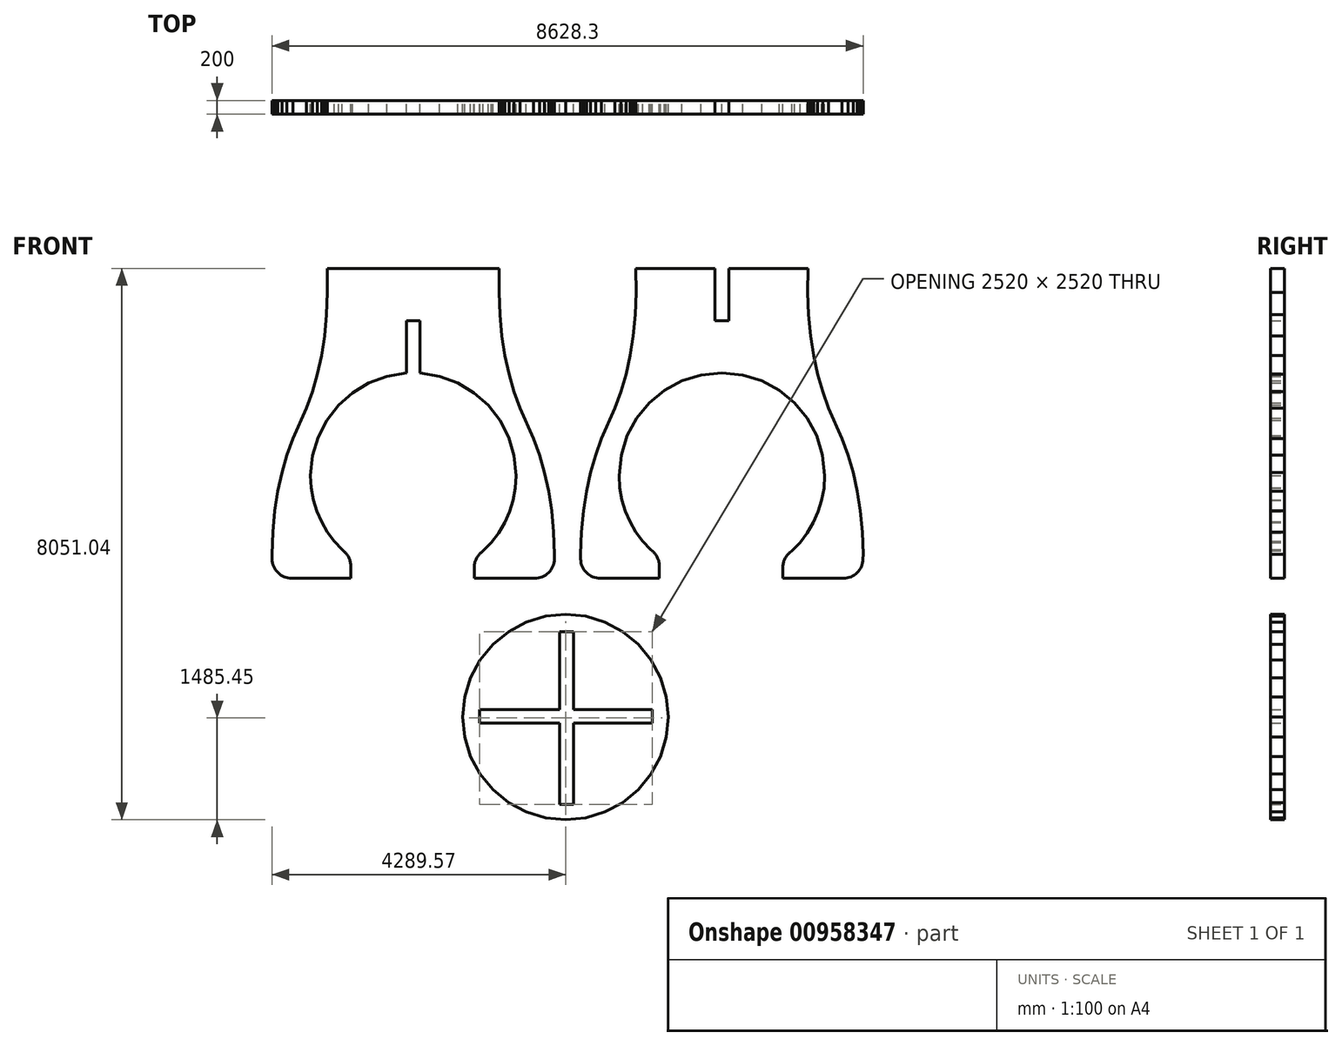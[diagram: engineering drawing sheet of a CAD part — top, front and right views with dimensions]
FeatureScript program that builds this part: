
annotation { "Feature Type Name" : "Feature", "Feature Type Description" : "" }
export const myFeature = defineFeature(function(context is Context, id is Id, definition is map)
    precondition{}
    {
        {
            var Q0;
            Q0=qCreatedBy(makeId("Front.planeOp"),FACE);
            var sketch = newSketch(context, id + "F0", { "sketchPlane" : qUnion([Q0])});
            skLineSegment(sketch, "E0", {"start": v(-5472.14, -2386.2) * mm, "end": v(-5169.83, -2416.68) * mm});
            skLineSegment(sketch, "E1", {"start": v(-5169.83, -2416.68) * mm, "end": v(-4888.27, -2504.08) * mm});
            skLineSegment(sketch, "E2", {"start": v(-4888.27, -2504.08) * mm, "end": v(-4633.47, -2642.38) * mm});
            skLineSegment(sketch, "E3", {"start": v(-4633.47, -2642.38) * mm, "end": v(-4411.48, -2825.54) * mm});
            skLineSegment(sketch, "E4", {"start": v(-4411.48, -2825.54) * mm, "end": v(-4228.31, -3047.54) * mm});
            skLineSegment(sketch, "E5", {"start": v(-4228.31, -3047.54) * mm, "end": v(-4090.01, -3302.33) * mm});
            skLineSegment(sketch, "E6", {"start": v(-4090.01, -3302.33) * mm, "end": v(-4002.61, -3583.9) * mm});
            skLineSegment(sketch, "E7", {"start": v(-4002.61, -3583.9) * mm, "end": v(-3972.14, -3886.2) * mm});
            skLineSegment(sketch, "E8", {"start": v(-3972.14, -3886.2) * mm, "end": v(-3983.21, -4069.37) * mm});
            skLineSegment(sketch, "E9", {"start": v(-3983.21, -4069.37) * mm, "end": v(-4015.57, -4245.97) * mm});
            skLineSegment(sketch, "E10", {"start": v(-4015.57, -4245.97) * mm, "end": v(-4067.92, -4414.7) * mm});
            skLineSegment(sketch, "E11", {"start": v(-4067.92, -4414.7) * mm, "end": v(-4138.96, -4574.27) * mm});
            skLineSegment(sketch, "E12", {"start": v(-4138.96, -4574.27) * mm, "end": v(-4227.4, -4723.4) * mm});
            skLineSegment(sketch, "E13", {"start": v(-4227.4, -4723.4) * mm, "end": v(-4331.93, -4860.76) * mm});
            skLineSegment(sketch, "E14", {"start": v(-4331.93, -4860.76) * mm, "end": v(-4451.26, -4985.1) * mm});
            skLineSegment(sketch, "E15", {"start": v(-4451.26, -4985.1) * mm, "end": v(-4584.1, -5095.1) * mm});
            skLineSegment(sketch, "E16", {"start": v(-4584.1, -5095.1) * mm, "end": v(-4584.1, -5386.56) * mm});
            skLineSegment(sketch, "E17", {"start": v(-4584.1, -5386.56) * mm, "end": v(-3416.13, -5386.56) * mm});
            skLineSegment(sketch, "E18", {"start": v(-3416.13, -5386.56) * mm, "end": v(-3411.1, -5036.82) * mm});
            skLineSegment(sketch, "E19", {"start": v(-3411.1, -5036.82) * mm, "end": v(-3423.6, -4708.36) * mm});
            skLineSegment(sketch, "E20", {"start": v(-3423.6, -4708.36) * mm, "end": v(-3452.73, -4400.09) * mm});
            skLineSegment(sketch, "E21", {"start": v(-3452.73, -4400.09) * mm, "end": v(-3497.58, -4110.9) * mm});
            skLineSegment(sketch, "E22", {"start": v(-3497.58, -4110.9) * mm, "end": v(-3557.24, -3839.7) * mm});
            skLineSegment(sketch, "E23", {"start": v(-3557.24, -3839.7) * mm, "end": v(-3630.82, -3585.4) * mm});
            skLineSegment(sketch, "E24", {"start": v(-3630.82, -3585.4) * mm, "end": v(-3717.4, -3346.9) * mm});
            skLineSegment(sketch, "E25", {"start": v(-3717.4, -3346.9) * mm, "end": v(-3816.1, -3123.12) * mm});
            skLineSegment(sketch, "E26", {"start": v(-3816.1, -3123.12) * mm, "end": v(-3914.8, -2899.32) * mm});
            skLineSegment(sketch, "E27", {"start": v(-3914.8, -2899.32) * mm, "end": v(-4001.4, -2660.83) * mm});
            skLineSegment(sketch, "E28", {"start": v(-4001.4, -2660.83) * mm, "end": v(-4074.97, -2406.53) * mm});
            skLineSegment(sketch, "E29", {"start": v(-4074.97, -2406.53) * mm, "end": v(-4134.64, -2135.33) * mm});
            skLineSegment(sketch, "E30", {"start": v(-4134.64, -2135.33) * mm, "end": v(-4179.48, -1846.15) * mm});
            skLineSegment(sketch, "E31", {"start": v(-4179.48, -1846.15) * mm, "end": v(-4208.6, -1537.87) * mm});
            skLineSegment(sketch, "E32", {"start": v(-4208.6, -1537.87) * mm, "end": v(-4221.11, -1209.4) * mm});
            skLineSegment(sketch, "E33", {"start": v(-4221.11, -1209.4) * mm, "end": v(-4216.09, -859.67) * mm});
            skLineSegment(sketch, "E34", {"start": v(-4216.09, -859.67) * mm, "end": v(-5372.12, -859.67) * mm});
            skLineSegment(sketch, "E35", {"start": v(-5372.12, -859.67) * mm, "end": v(-5372.12, -1622.94) * mm});
            skLineSegment(sketch, "E36", {"start": v(-5372.12, -1622.94) * mm, "end": v(-5572.12, -1622.94) * mm});
            skLineSegment(sketch, "E37", {"start": v(-5572.12, -1622.94) * mm, "end": v(-5572.12, -859.67) * mm});
            skLineSegment(sketch, "E38", {"start": v(-5572.12, -859.67) * mm, "end": v(-6730.15, -859.67) * mm});
            skLineSegment(sketch, "E39", {"start": v(-6730.15, -859.67) * mm, "end": v(-6725.13, -1209.4) * mm});
            skLineSegment(sketch, "E40", {"start": v(-6725.13, -1209.4) * mm, "end": v(-6737.64, -1537.87) * mm});
            skLineSegment(sketch, "E41", {"start": v(-6737.64, -1537.87) * mm, "end": v(-6766.76, -1846.15) * mm});
            skLineSegment(sketch, "E42", {"start": v(-6766.76, -1846.15) * mm, "end": v(-6811.6, -2135.33) * mm});
            skLineSegment(sketch, "E43", {"start": v(-6811.6, -2135.33) * mm, "end": v(-6871.27, -2406.53) * mm});
            skLineSegment(sketch, "E44", {"start": v(-6871.27, -2406.53) * mm, "end": v(-6944.85, -2660.83) * mm});
            skLineSegment(sketch, "E45", {"start": v(-6944.85, -2660.83) * mm, "end": v(-7031.44, -2899.32) * mm});
            skLineSegment(sketch, "E46", {"start": v(-7031.44, -2899.32) * mm, "end": v(-7130.14, -3123.12) * mm});
            skLineSegment(sketch, "E47", {"start": v(-7130.14, -3123.12) * mm, "end": v(-7228.84, -3346.9) * mm});
            skLineSegment(sketch, "E48", {"start": v(-7228.84, -3346.9) * mm, "end": v(-7315.42, -3585.4) * mm});
            skLineSegment(sketch, "E49", {"start": v(-7315.42, -3585.4) * mm, "end": v(-7389, -3839.7) * mm});
            skLineSegment(sketch, "E50", {"start": v(-7389, -3839.7) * mm, "end": v(-7448.66, -4110.9) * mm});
            skLineSegment(sketch, "E51", {"start": v(-7448.66, -4110.9) * mm, "end": v(-7493.5, -4400.09) * mm});
            skLineSegment(sketch, "E52", {"start": v(-7493.5, -4400.09) * mm, "end": v(-7522.63, -4708.36) * mm});
            skLineSegment(sketch, "E53", {"start": v(-7522.63, -4708.36) * mm, "end": v(-7535.14, -5036.82) * mm});
            skLineSegment(sketch, "E54", {"start": v(-7535.14, -5036.82) * mm, "end": v(-7530.12, -5386.56) * mm});
            skLineSegment(sketch, "E55", {"start": v(-7530.12, -5386.56) * mm, "end": v(-6384.1, -5386.56) * mm});
            skLineSegment(sketch, "E56", {"start": v(-6384.1, -5386.56) * mm, "end": v(-6384.1, -5077.1) * mm});
            skLineSegment(sketch, "E57", {"start": v(-6384.1, -5077.1) * mm, "end": v(-6512, -4967.11) * mm});
            skLineSegment(sketch, "E58", {"start": v(-6512, -4967.11) * mm, "end": v(-6626.8, -4843.6) * mm});
            skLineSegment(sketch, "E59", {"start": v(-6626.8, -4843.6) * mm, "end": v(-6727.26, -4707.77) * mm});
            skLineSegment(sketch, "E60", {"start": v(-6727.26, -4707.77) * mm, "end": v(-6812.18, -4560.83) * mm});
            skLineSegment(sketch, "E61", {"start": v(-6812.18, -4560.83) * mm, "end": v(-6880.34, -4404) * mm});
            skLineSegment(sketch, "E62", {"start": v(-6880.34, -4404) * mm, "end": v(-6930.53, -4238.47) * mm});
            skLineSegment(sketch, "E63", {"start": v(-6930.53, -4238.47) * mm, "end": v(-6961.53, -4065.47) * mm});
            skLineSegment(sketch, "E64", {"start": v(-6961.53, -4065.47) * mm, "end": v(-6972.14, -3886.2) * mm});
            skLineSegment(sketch, "E65", {"start": v(-6972.14, -3886.2) * mm, "end": v(-6941.66, -3583.9) * mm});
            skLineSegment(sketch, "E66", {"start": v(-6941.66, -3583.9) * mm, "end": v(-6854.26, -3302.33) * mm});
            skLineSegment(sketch, "E67", {"start": v(-6854.26, -3302.33) * mm, "end": v(-6715.96, -3047.54) * mm});
            skLineSegment(sketch, "E68", {"start": v(-6715.96, -3047.54) * mm, "end": v(-6532.8, -2825.54) * mm});
            skLineSegment(sketch, "E69", {"start": v(-6532.8, -2825.54) * mm, "end": v(-6310.8, -2642.38) * mm});
            skLineSegment(sketch, "E70", {"start": v(-6310.8, -2642.38) * mm, "end": v(-6056, -2504.08) * mm});
            skLineSegment(sketch, "E71", {"start": v(-6056, -2504.08) * mm, "end": v(-5774.44, -2416.68) * mm});
            skLineSegment(sketch, "E72", {"start": v(-5774.44, -2416.68) * mm, "end": v(-5472.14, -2386.2) * mm});
            skLineSegment(sketch, "E73", {"start": v(-9877.4, -2389.54) * mm, "end": v(-9592.6, -2435.87) * mm});
            skLineSegment(sketch, "E74", {"start": v(-9592.6, -2435.87) * mm, "end": v(-9328.48, -2533.08) * mm});
            skLineSegment(sketch, "E75", {"start": v(-9328.48, -2533.08) * mm, "end": v(-9090.35, -2675.84) * mm});
            skLineSegment(sketch, "E76", {"start": v(-9090.35, -2675.84) * mm, "end": v(-8883.56, -2858.8) * mm});
            skLineSegment(sketch, "E77", {"start": v(-8883.56, -2858.8) * mm, "end": v(-8713.43, -3076.66) * mm});
            skLineSegment(sketch, "E78", {"start": v(-8713.43, -3076.66) * mm, "end": v(-8585.3, -3324.06) * mm});
            skLineSegment(sketch, "E79", {"start": v(-8585.3, -3324.06) * mm, "end": v(-8504.52, -3595.69) * mm});
            skLineSegment(sketch, "E80", {"start": v(-8504.52, -3595.69) * mm, "end": v(-8476.4, -3886.2) * mm});
            skLineSegment(sketch, "E81", {"start": v(-8476.4, -3886.2) * mm, "end": v(-8487.48, -4069.37) * mm});
            skLineSegment(sketch, "E82", {"start": v(-8487.48, -4069.37) * mm, "end": v(-8519.84, -4245.97) * mm});
            skLineSegment(sketch, "E83", {"start": v(-8519.84, -4245.97) * mm, "end": v(-8572.19, -4414.7) * mm});
            skLineSegment(sketch, "E84", {"start": v(-8572.19, -4414.7) * mm, "end": v(-8643.23, -4574.27) * mm});
            skLineSegment(sketch, "E85", {"start": v(-8643.23, -4574.27) * mm, "end": v(-8731.66, -4723.4) * mm});
            skLineSegment(sketch, "E86", {"start": v(-8731.66, -4723.4) * mm, "end": v(-8836.2, -4860.76) * mm});
            skLineSegment(sketch, "E87", {"start": v(-8836.2, -4860.76) * mm, "end": v(-8955.53, -4985.1) * mm});
            skLineSegment(sketch, "E88", {"start": v(-8955.53, -4985.1) * mm, "end": v(-9088.37, -5095.1) * mm});
            skLineSegment(sketch, "E89", {"start": v(-9088.37, -5095.1) * mm, "end": v(-9088.37, -5386.56) * mm});
            skLineSegment(sketch, "E90", {"start": v(-9088.37, -5386.56) * mm, "end": v(-7920.4, -5386.56) * mm});
            skLineSegment(sketch, "E91", {"start": v(-7920.4, -5386.56) * mm, "end": v(-7915.37, -5036.82) * mm});
            skLineSegment(sketch, "E92", {"start": v(-7915.37, -5036.82) * mm, "end": v(-7927.87, -4708.36) * mm});
            skLineSegment(sketch, "E93", {"start": v(-7927.87, -4708.36) * mm, "end": v(-7957, -4400.09) * mm});
            skLineSegment(sketch, "E94", {"start": v(-7957, -4400.09) * mm, "end": v(-8001.84, -4110.9) * mm});
            skLineSegment(sketch, "E95", {"start": v(-8001.84, -4110.9) * mm, "end": v(-8061.5, -3839.7) * mm});
            skLineSegment(sketch, "E96", {"start": v(-8061.5, -3839.7) * mm, "end": v(-8135.08, -3585.4) * mm});
            skLineSegment(sketch, "E97", {"start": v(-8135.08, -3585.4) * mm, "end": v(-8221.67, -3346.9) * mm});
            skLineSegment(sketch, "E98", {"start": v(-8221.67, -3346.9) * mm, "end": v(-8320.37, -3123.12) * mm});
            skLineSegment(sketch, "E99", {"start": v(-8320.37, -3123.12) * mm, "end": v(-8419.07, -2899.32) * mm});
            skLineSegment(sketch, "E100", {"start": v(-8419.07, -2899.32) * mm, "end": v(-8505.66, -2660.83) * mm});
            skLineSegment(sketch, "E101", {"start": v(-8505.66, -2660.83) * mm, "end": v(-8579.24, -2406.53) * mm});
            skLineSegment(sketch, "E102", {"start": v(-8579.24, -2406.53) * mm, "end": v(-8638.9, -2135.33) * mm});
            skLineSegment(sketch, "E103", {"start": v(-8638.9, -2135.33) * mm, "end": v(-8683.75, -1846.15) * mm});
            skLineSegment(sketch, "E104", {"start": v(-8683.75, -1846.15) * mm, "end": v(-8712.87, -1537.87) * mm});
            skLineSegment(sketch, "E105", {"start": v(-8712.87, -1537.87) * mm, "end": v(-8725.38, -1209.4) * mm});
            skLineSegment(sketch, "E106", {"start": v(-8725.38, -1209.4) * mm, "end": v(-8720.36, -859.67) * mm});
            skLineSegment(sketch, "E107", {"start": v(-8720.36, -859.67) * mm, "end": v(-11234.42, -859.67) * mm});
            skLineSegment(sketch, "E108", {"start": v(-11234.42, -859.67) * mm, "end": v(-11229.4, -1209.4) * mm});
            skLineSegment(sketch, "E109", {"start": v(-11229.4, -1209.4) * mm, "end": v(-11241.9, -1537.87) * mm});
            skLineSegment(sketch, "E110", {"start": v(-11241.9, -1537.87) * mm, "end": v(-11271.03, -1846.15) * mm});
            skLineSegment(sketch, "E111", {"start": v(-11271.03, -1846.15) * mm, "end": v(-11315.87, -2135.33) * mm});
            skLineSegment(sketch, "E112", {"start": v(-11315.87, -2135.33) * mm, "end": v(-11375.53, -2406.53) * mm});
            skLineSegment(sketch, "E113", {"start": v(-11375.53, -2406.53) * mm, "end": v(-11449.11, -2660.83) * mm});
            skLineSegment(sketch, "E114", {"start": v(-11449.11, -2660.83) * mm, "end": v(-11535.7, -2899.32) * mm});
            skLineSegment(sketch, "E115", {"start": v(-11535.7, -2899.32) * mm, "end": v(-11634.4, -3123.12) * mm});
            skLineSegment(sketch, "E116", {"start": v(-11634.4, -3123.12) * mm, "end": v(-11733.1, -3346.9) * mm});
            skLineSegment(sketch, "E117", {"start": v(-11733.1, -3346.9) * mm, "end": v(-11819.7, -3585.4) * mm});
            skLineSegment(sketch, "E118", {"start": v(-11819.7, -3585.4) * mm, "end": v(-11893.27, -3839.7) * mm});
            skLineSegment(sketch, "E119", {"start": v(-11893.27, -3839.7) * mm, "end": v(-11952.93, -4110.9) * mm});
            skLineSegment(sketch, "E120", {"start": v(-11952.93, -4110.9) * mm, "end": v(-11997.78, -4400.09) * mm});
            skLineSegment(sketch, "E121", {"start": v(-11997.78, -4400.09) * mm, "end": v(-12026.9, -4708.36) * mm});
            skLineSegment(sketch, "E122", {"start": v(-12026.9, -4708.36) * mm, "end": v(-12039.4, -5036.82) * mm});
            skLineSegment(sketch, "E123", {"start": v(-12039.4, -5036.82) * mm, "end": v(-12034.38, -5386.56) * mm});
            skLineSegment(sketch, "E124", {"start": v(-12034.38, -5386.56) * mm, "end": v(-10888.37, -5386.56) * mm});
            skLineSegment(sketch, "E125", {"start": v(-10888.37, -5386.56) * mm, "end": v(-10888.37, -5077.1) * mm});
            skLineSegment(sketch, "E126", {"start": v(-10888.37, -5077.1) * mm, "end": v(-11016.27, -4967.11) * mm});
            skLineSegment(sketch, "E127", {"start": v(-11016.27, -4967.11) * mm, "end": v(-11131.06, -4843.6) * mm});
            skLineSegment(sketch, "E128", {"start": v(-11131.06, -4843.6) * mm, "end": v(-11231.52, -4707.77) * mm});
            skLineSegment(sketch, "E129", {"start": v(-11231.52, -4707.77) * mm, "end": v(-11316.44, -4560.83) * mm});
            skLineSegment(sketch, "E130", {"start": v(-11316.44, -4560.83) * mm, "end": v(-11384.6, -4404) * mm});
            skLineSegment(sketch, "E131", {"start": v(-11384.6, -4404) * mm, "end": v(-11434.8, -4238.47) * mm});
            skLineSegment(sketch, "E132", {"start": v(-11434.8, -4238.47) * mm, "end": v(-11465.8, -4065.47) * mm});
            skLineSegment(sketch, "E133", {"start": v(-11465.8, -4065.47) * mm, "end": v(-11476.4, -3886.2) * mm});
            skLineSegment(sketch, "E134", {"start": v(-11476.4, -3886.2) * mm, "end": v(-11448.34, -3595.93) * mm});
            skLineSegment(sketch, "E135", {"start": v(-11448.34, -3595.93) * mm, "end": v(-11367.68, -3324.5) * mm});
            skLineSegment(sketch, "E136", {"start": v(-11367.68, -3324.5) * mm, "end": v(-11239.76, -3077.25) * mm});
            skLineSegment(sketch, "E137", {"start": v(-11239.76, -3077.25) * mm, "end": v(-11069.9, -2859.5) * mm});
            skLineSegment(sketch, "E138", {"start": v(-11069.9, -2859.5) * mm, "end": v(-10863.4, -2676.53) * mm});
            skLineSegment(sketch, "E139", {"start": v(-10863.4, -2676.53) * mm, "end": v(-10625.62, -2533.7) * mm});
            skLineSegment(sketch, "E140", {"start": v(-10625.62, -2533.7) * mm, "end": v(-10361.84, -2436.3) * mm});
            skLineSegment(sketch, "E141", {"start": v(-10361.84, -2436.3) * mm, "end": v(-10077.4, -2389.66) * mm});
            skLineSegment(sketch, "E142", {"start": v(-10077.4, -2389.66) * mm, "end": v(-10077.4, -1622.93) * mm});
            skLineSegment(sketch, "E143", {"start": v(-10077.4, -1622.93) * mm, "end": v(-9877.4, -1622.93) * mm});
            skLineSegment(sketch, "E144", {"start": v(-9877.4, -1622.93) * mm, "end": v(-9877.4, -2389.54) * mm});
            skLineSegment(sketch, "E145", {"start": v(-7753.7, -5910.71) * mm, "end": v(-8046.33, -5939.54) * mm});
            skLineSegment(sketch, "E146", {"start": v(-8046.33, -5939.54) * mm, "end": v(-8327.72, -6024.9) * mm});
            skLineSegment(sketch, "E147", {"start": v(-8327.72, -6024.9) * mm, "end": v(-8587.05, -6163.5) * mm});
            skLineSegment(sketch, "E148", {"start": v(-8587.05, -6163.5) * mm, "end": v(-8814.35, -6350.05) * mm});
            skLineSegment(sketch, "E149", {"start": v(-8814.35, -6350.05) * mm, "end": v(-9000.9, -6577.36) * mm});
            skLineSegment(sketch, "E150", {"start": v(-9000.9, -6577.36) * mm, "end": v(-9139.51, -6836.69) * mm});
            skLineSegment(sketch, "E151", {"start": v(-9139.51, -6836.69) * mm, "end": v(-9224.87, -7118.08) * mm});
            skLineSegment(sketch, "E152", {"start": v(-9224.87, -7118.08) * mm, "end": v(-9253.7, -7410.71) * mm});
            skLineSegment(sketch, "E153", {"start": v(-9253.7, -7410.71) * mm, "end": v(-9224.87, -7703.35) * mm});
            skLineSegment(sketch, "E154", {"start": v(-9224.87, -7703.35) * mm, "end": v(-9139.51, -7984.74) * mm});
            skLineSegment(sketch, "E155", {"start": v(-9139.51, -7984.74) * mm, "end": v(-9000.9, -8244.07) * mm});
            skLineSegment(sketch, "E156", {"start": v(-9000.9, -8244.07) * mm, "end": v(-8814.35, -8471.37) * mm});
            skLineSegment(sketch, "E157", {"start": v(-8814.35, -8471.37) * mm, "end": v(-8587.05, -8657.92) * mm});
            skLineSegment(sketch, "E158", {"start": v(-8587.05, -8657.92) * mm, "end": v(-8327.72, -8796.53) * mm});
            skLineSegment(sketch, "E159", {"start": v(-8327.72, -8796.53) * mm, "end": v(-8046.33, -8881.9) * mm});
            skLineSegment(sketch, "E160", {"start": v(-8046.33, -8881.9) * mm, "end": v(-7753.7, -8910.71) * mm});
            skLineSegment(sketch, "E161", {"start": v(-7753.7, -8910.71) * mm, "end": v(-7461.06, -8881.9) * mm});
            skLineSegment(sketch, "E162", {"start": v(-7461.06, -8881.9) * mm, "end": v(-7179.67, -8796.53) * mm});
            skLineSegment(sketch, "E163", {"start": v(-7179.67, -8796.53) * mm, "end": v(-6920.34, -8657.92) * mm});
            skLineSegment(sketch, "E164", {"start": v(-6920.34, -8657.92) * mm, "end": v(-6693.03, -8471.37) * mm});
            skLineSegment(sketch, "E165", {"start": v(-6693.03, -8471.37) * mm, "end": v(-6506.49, -8244.07) * mm});
            skLineSegment(sketch, "E166", {"start": v(-6506.49, -8244.07) * mm, "end": v(-6367.87, -7984.74) * mm});
            skLineSegment(sketch, "E167", {"start": v(-6367.87, -7984.74) * mm, "end": v(-6282.52, -7703.35) * mm});
            skLineSegment(sketch, "E168", {"start": v(-6282.52, -7703.35) * mm, "end": v(-6253.7, -7410.71) * mm});
            skLineSegment(sketch, "E169", {"start": v(-6253.7, -7410.71) * mm, "end": v(-6282.52, -7118.08) * mm});
            skLineSegment(sketch, "E170", {"start": v(-6282.52, -7118.08) * mm, "end": v(-6367.87, -6836.69) * mm});
            skLineSegment(sketch, "E171", {"start": v(-6367.87, -6836.69) * mm, "end": v(-6506.49, -6577.36) * mm});
            skLineSegment(sketch, "E172", {"start": v(-6506.49, -6577.36) * mm, "end": v(-6693.03, -6350.05) * mm});
            skLineSegment(sketch, "E173", {"start": v(-6693.03, -6350.05) * mm, "end": v(-6920.34, -6163.5) * mm});
            skLineSegment(sketch, "E174", {"start": v(-6920.34, -6163.5) * mm, "end": v(-7179.67, -6024.9) * mm});
            skLineSegment(sketch, "E175", {"start": v(-7179.67, -6024.9) * mm, "end": v(-7461.06, -5939.54) * mm});
            skLineSegment(sketch, "E176", {"start": v(-7461.06, -5939.54) * mm, "end": v(-7753.7, -5910.71) * mm});
            skSolve(sketch);
        }
        {
            var Q0;
            Q0=qSketchRegion(id+"F0",true);
            extrude(context, id + "F1", {"entities" : qUnion([Q0]), "depth" : 200 * mm, "offsetDistance" : 25 * mm});
        }
        {
            var Q0;
            Q0=makeQuery(id+"F1.opExtrude","SWEPT_EDGE",EDGE,{"disambiguationData":[OSD([sQuery(id+"F0.wireOp",EDGE,"E123"),sQuery(id+"F0.wireOp",EDGE,"E124")])]});
            var Q1;
            Q1=makeQuery(id+"F1.opExtrude","SWEPT_EDGE",EDGE,{"disambiguationData":[OSD([sQuery(id+"F0.wireOp",EDGE,"E90"),sQuery(id+"F0.wireOp",EDGE,"E91")])]});
            var Q2;
            Q2=makeQuery(id+"F1.opExtrude","SWEPT_EDGE",EDGE,{"disambiguationData":[OSD([sQuery(id+"F0.wireOp",EDGE,"E54"),sQuery(id+"F0.wireOp",EDGE,"E55")])]});
            var Q3;
            Q3=makeQuery(id+"F1.opExtrude","SWEPT_EDGE",EDGE,{"disambiguationData":[OSD([sQuery(id+"F0.wireOp",EDGE,"E17"),sQuery(id+"F0.wireOp",EDGE,"E18")])]});
            var Q4;
            Q4=makeQuery(id+"F1.opExtrude","SWEPT_EDGE",EDGE,{"disambiguationData":[OSD([sQuery(id+"F0.wireOp",EDGE,"E15"),sQuery(id+"F0.wireOp",EDGE,"E16")])]});
            var Q5;
            Q5=makeQuery(id+"F1.opExtrude","SWEPT_EDGE",EDGE,{"disambiguationData":[OSD([sQuery(id+"F0.wireOp",EDGE,"E56"),sQuery(id+"F0.wireOp",EDGE,"E57")])]});
            var Q6;
            Q6=makeQuery(id+"F1.opExtrude","SWEPT_EDGE",EDGE,{"disambiguationData":[OSD([sQuery(id+"F0.wireOp",EDGE,"E88"),sQuery(id+"F0.wireOp",EDGE,"E89")])]});
            var Q7;
            Q7=makeQuery(id+"F1.opExtrude","SWEPT_EDGE",EDGE,{"disambiguationData":[OSD([sQuery(id+"F0.wireOp",EDGE,"E125"),sQuery(id+"F0.wireOp",EDGE,"E126")])]});
            fillet(context, id + "F2", {"entities" : qUnion([Q0, Q1, Q2, Q3, Q4, Q5, Q6, Q7]), "radius" : 289.04 * mm, "tangentPropagation" : true, "allowEdgeOverflow" : false});
        }
        {
            var Q0;
            Q0=qCreatedBy(makeId("Front.planeOp"),FACE);
            var sketch = newSketch(context, id + "F3", { "sketchPlane" : qUnion([Q0])});
            skLineSegment(sketch, "E177.bottom", {"start": v(-9009.83, -7300) * mm, "end": v(-6489.83, -7300) * mm});
            skLineSegment(sketch, "E177.top", {"start": v(-9009.83, -7500) * mm, "end": v(-6489.83, -7500) * mm});
            skLineSegment(sketch, "E177.left", {"start": v(-9009.83, -7300) * mm, "end": v(-9009.83, -7500) * mm});
            skLineSegment(sketch, "E177.right", {"start": v(-6489.83, -7300) * mm, "end": v(-6489.83, -7500) * mm});
            skLineSegment(sketch, "E178.bottom", {"start": v(-7840, -8685.26) * mm, "end": v(-7840, -6165.26) * mm});
            skLineSegment(sketch, "E178.top", {"start": v(-7640, -8685.26) * mm, "end": v(-7640, -6165.26) * mm});
            skLineSegment(sketch, "E178.left", {"start": v(-7840, -8685.26) * mm, "end": v(-7640, -8685.26) * mm});
            skLineSegment(sketch, "E178.right", {"start": v(-7840, -6165.26) * mm, "end": v(-7640, -6165.26) * mm});
            skSolve(sketch);
        }
        {
            var Q0;
            Q0=qSketchRegion(id+"F3",true);
            extrude(context, id + "F4", {"entities" : qUnion([Q0]), "operationType" : NewBodyOperationType.REMOVE, "depth" : 810 * mm, "offsetDistance" : 25 * mm});
        }
    });
